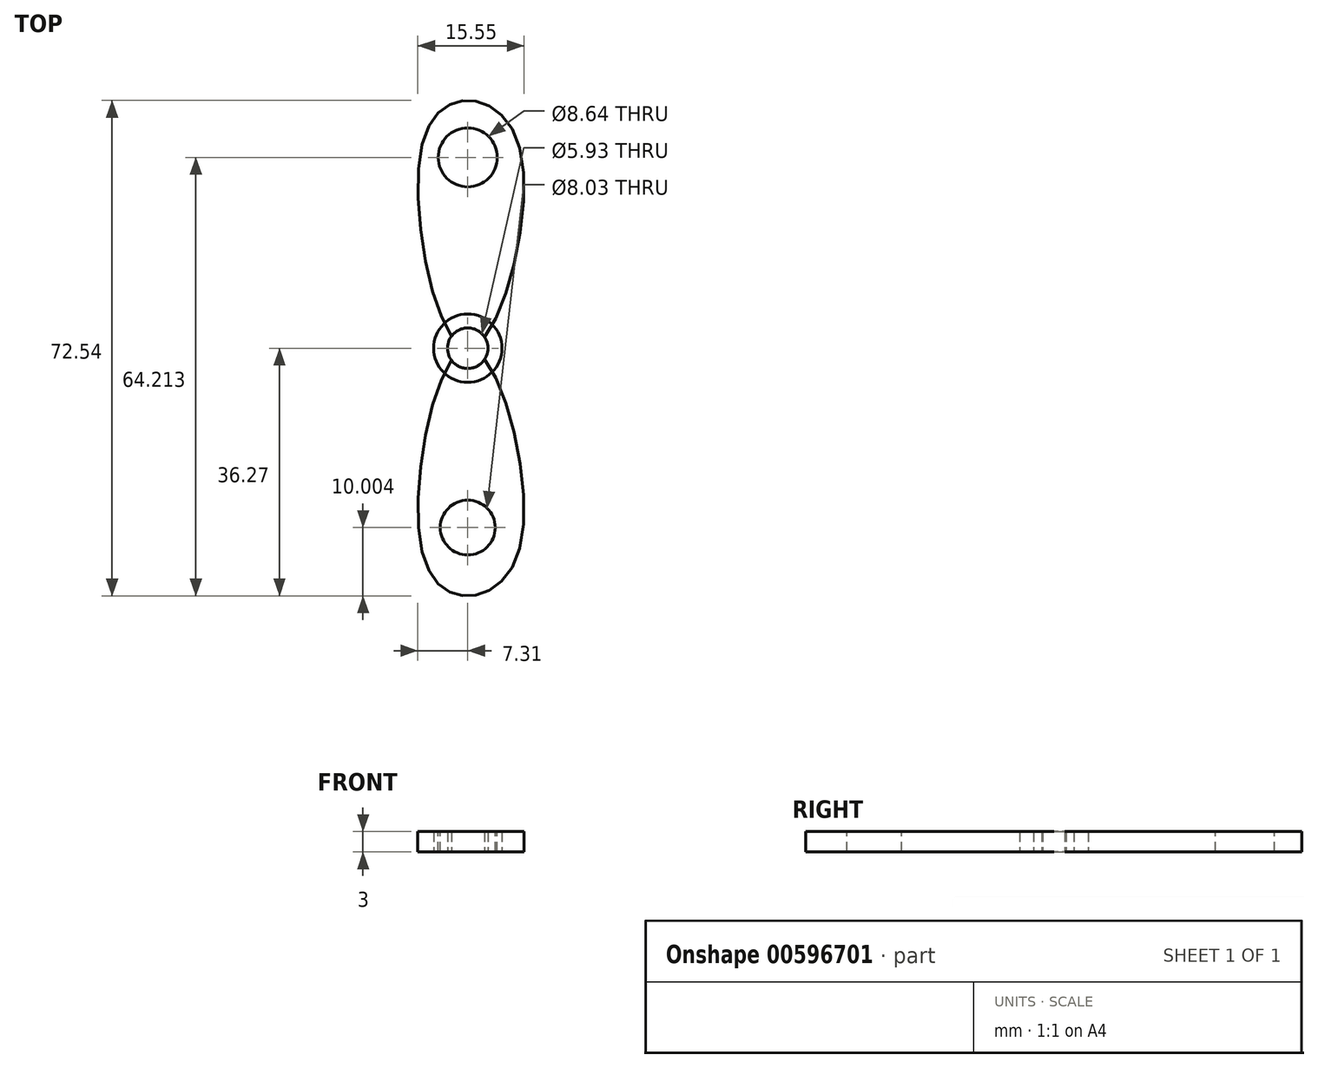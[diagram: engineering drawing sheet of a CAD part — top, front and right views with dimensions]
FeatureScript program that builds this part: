
annotation { "Feature Type Name" : "Feature", "Feature Type Description" : "" }
export const myFeature = defineFeature(function(context is Context, id is Id, definition is map)
    precondition{}
    {
        {
            var Q0;
            Q0=qCreatedBy(makeId("Top.planeOp"),FACE);
            var sketch = newSketch(context, id + "F0", { "sketchPlane" : qUnion([Q0])});
            skCircle(sketch, "E0", {"center": v(0, 0) * mm, "radius": 5 * mm});
            skSolve(sketch);
        }
        {
            var Q0;
            Q0=makeQuery(id+"F0.imprint","IMPRINT",FACE,{"disambiguationData":[TD([[makeQuery(id+"F0.imprint","IMPRINT",EDGE,{"derivedFrom":sQuery(id+"F0.wireOp",EDGE,"E0")}),1.0]])]});
            var sketch = newSketch(context, id + "F1", { "sketchPlane" : qUnion([Q0])});
            skFitSpline(sketch, "E1", {"points": [v(0, 0) * mm, v(-6.98, 28.4) * mm, v(0, 36.27) * mm, v(7.96, 27.62) * mm, v(0, 0) * mm]});
            skPoint(sketch, "E2.2.internal.orphan", {"position": v(0, -36.08) * mm});
            skLineSegment(sketch, "E3", {"start": v(0, 0) * mm, "end": v(32.93, 0) * mm});
            skFitSpline(sketch, "E4.MirrorC", {"points": [v(0, 0) * mm, v(-6.98, -28.4) * mm, v(0, -36.27) * mm, v(7.96, -27.62) * mm, v(0, 0) * mm]});
            skSolve(sketch);
        }
        {
            var Q0;
            Q0 = qSketchRegion(id + "F0", true);
            var Q1;
            Q1 = qSketchRegion(id + "F1", true);
            extrude(context, id + "F2", {"entities" : qUnion([Q0, Q1]), "depth" : 3 * mm, "offsetDistance" : 25 * mm});
        }
        {
            var Q0;
            Q0=makeQuery(id+"F2.opExtrude","CAP_FACE",FACE,{"disambiguationData":[OSD([sQuery(id+"F0.wireOp",EDGE,"E0")])],"isStart":true});
            var sketch = newSketch(context, id + "F3", { "sketchPlane" : qUnion([Q0])});
            skCircle(sketch, "E5", {"center": v(0, 0) * mm, "radius": 2.97 * mm});
            skSolve(sketch);
        }
        {
            var Q0;
            Q0=makeQuery(id+"F3.imprint","IMPRINT",FACE,{"disambiguationData":[TD([[makeQuery(id+"F3.imprint","IMPRINT",EDGE,{"derivedFrom":sQuery(id+"F3.wireOp",EDGE,"E5")}),1.0]])]});
            extrude(context, id + "F4", {"entities" : qUnion([Q0]), "operationType" : NewBodyOperationType.REMOVE, "oppositeDirection" : true, "depth" : 3 * mm, "offsetDistance" : 25 * mm});
        }
        {
            var Q0;
            {var subQ0=sQuery(id+"F1.wireOp",EDGE,"E1");Q0=makeQuery(id+"F4.boolean.opBoolean","SPLIT",FACE,{"disambiguationData":[TD([makeQuery(id+"F2.opExtrude","SWEPT_FACE",FACE,{"disambiguationData":[OSD([subQ0])]})])],"derivedFrom":makeQuery(id+"F2.opExtrude","CAP_FACE",FACE,{"disambiguationData":[OSD([subQ0,sQuery(id+"F1.wireOp",EDGE,"E4.MirrorC")])],"isStart":false})});}
            var sketch = newSketch(context, id + "F5", { "sketchPlane" : qUnion([Q0])});
            skCircle(sketch, "E6", {"center": v(0, 27.94) * mm, "radius": 4.32 * mm});
            skSolve(sketch);
        }
        {
            var Q0;
            Q0=makeQuery(id+"F5.imprint","IMPRINT",FACE,{"disambiguationData":[TD([[makeQuery(id+"F5.imprint","IMPRINT",EDGE,{"derivedFrom":sQuery(id+"F5.wireOp",EDGE,"E6")}),1.0]])]});
            extrude(context, id + "F6", {"entities" : qUnion([Q0]), "operationType" : NewBodyOperationType.REMOVE, "oppositeDirection" : true, "depth" : 3 * mm, "offsetDistance" : 25 * mm});
        }
        {
            var Q0;
            {var subQ0=sQuery(id+"F1.wireOp",EDGE,"E4.MirrorC");Q0=makeQuery(id+"F4.boolean.opBoolean","SPLIT",FACE,{"disambiguationData":[TD([makeQuery(id+"F2.opExtrude","SWEPT_FACE",FACE,{"disambiguationData":[OSD([subQ0])]})])],"derivedFrom":makeQuery(id+"F2.opExtrude","CAP_FACE",FACE,{"disambiguationData":[OSD([sQuery(id+"F1.wireOp",EDGE,"E1"),subQ0])],"isStart":false})});}
            var sketch = newSketch(context, id + "F7", { "sketchPlane" : qUnion([Q0])});
            skCircle(sketch, "E7", {"center": v(0, -26.27) * mm, "radius": 4.01 * mm});
            skCircle(sketch, "E8.MirrorC", {"center": v(0, 26.27) * mm, "radius": 4.01 * mm});
            skSolve(sketch);
        }
        {
            var Q0;
            Q0=makeQuery(id+"F7.imprint","IMPRINT",FACE,{"disambiguationData":[TD([[makeQuery(id+"F7.imprint","IMPRINT",EDGE,{"derivedFrom":sQuery(id+"F7.wireOp",EDGE,"E7")}),1.0]])]});
            extrude(context, id + "F8", {"entities" : qUnion([Q0]), "operationType" : NewBodyOperationType.REMOVE, "oppositeDirection" : true, "depth" : 3 * mm, "offsetDistance" : 25 * mm});
        }
    });
